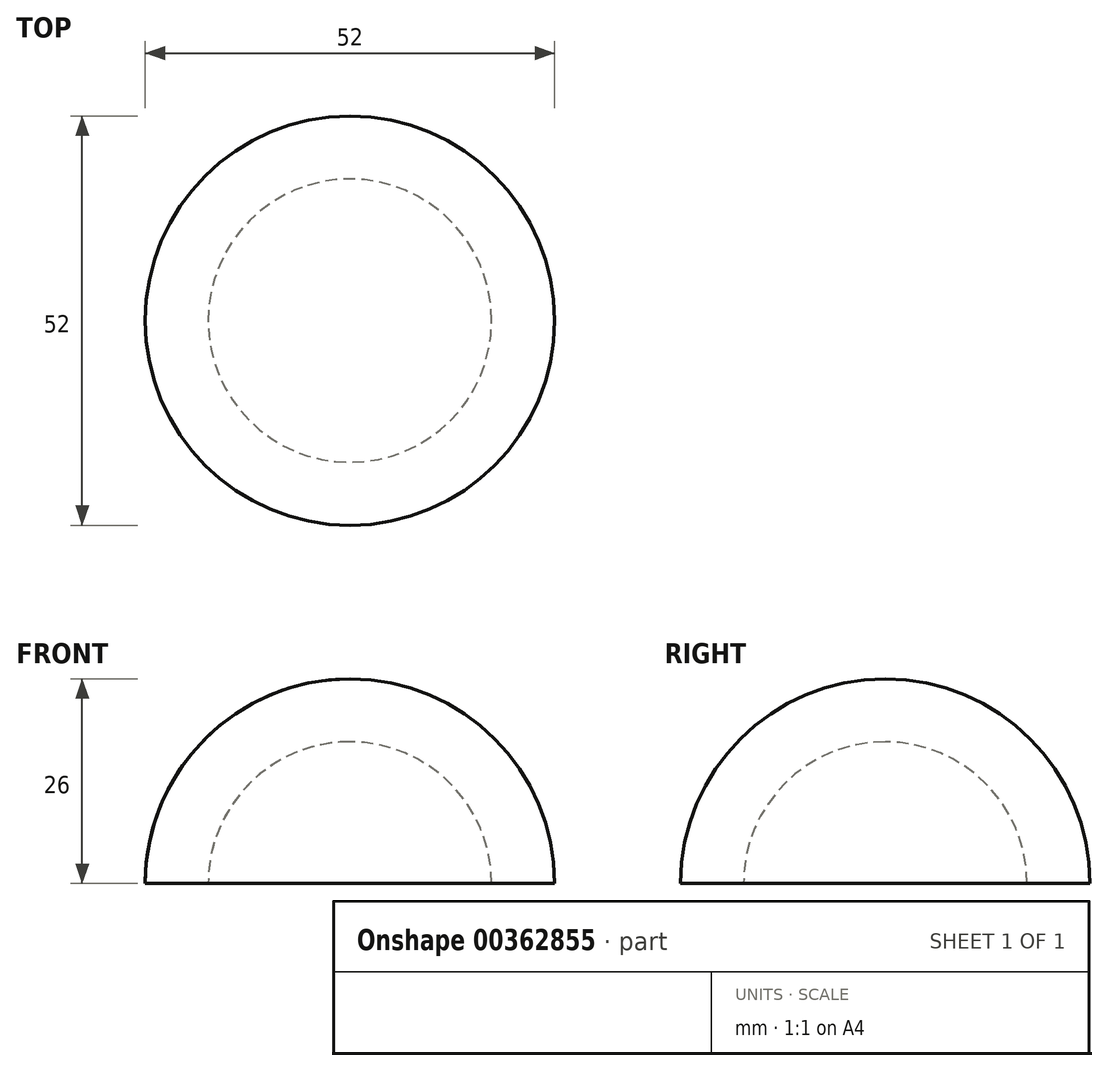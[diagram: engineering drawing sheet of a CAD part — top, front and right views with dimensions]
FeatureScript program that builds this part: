
annotation { "Feature Type Name" : "Feature", "Feature Type Description" : "" }
export const myFeature = defineFeature(function(context is Context, id is Id, definition is map)
    precondition{}
    {
        {
            var Q0;
            Q0=qCreatedBy(makeId("Front.planeOp"),FACE);
            var sketch = newSketch(context, id + "F0", { "sketchPlane" : qUnion([Q0])});
            skArc(sketch, "E0", {"start": v(-26, 0) * mm, "mid": v(-18.38, 18.38) * mm, "end": v(0, 26) * mm});
            skArc(sketch, "E1", {"start": v(0, 18) * mm, "mid": v(-12.73, 12.73) * mm, "end": v(-18, 0) * mm});
            skLineSegment(sketch, "E2", {"start": v(-26, 0) * mm, "end": v(-18, 0) * mm});
            skLineSegment(sketch, "E3", {"start": v(0, 0) * mm, "end": v(0, 26) * mm, "construction": true});
            skLineSegment(sketch, "E4", {"start": v(0, 26) * mm, "end": v(0, 18) * mm});
            skSolve(sketch);
        }
        {
            var Q0;
            Q0 = qSketchRegion(id + "F0", true);
            var Q1;
            Q1=sQuery(id+"F0.wireOp",EDGE,"E3");
            revolve(context, id + "F1", {"entities" : qUnion([Q0]), "axis" : qUnion([Q1]), "revolveType" : RevolveType.FULL});
        }
    });
